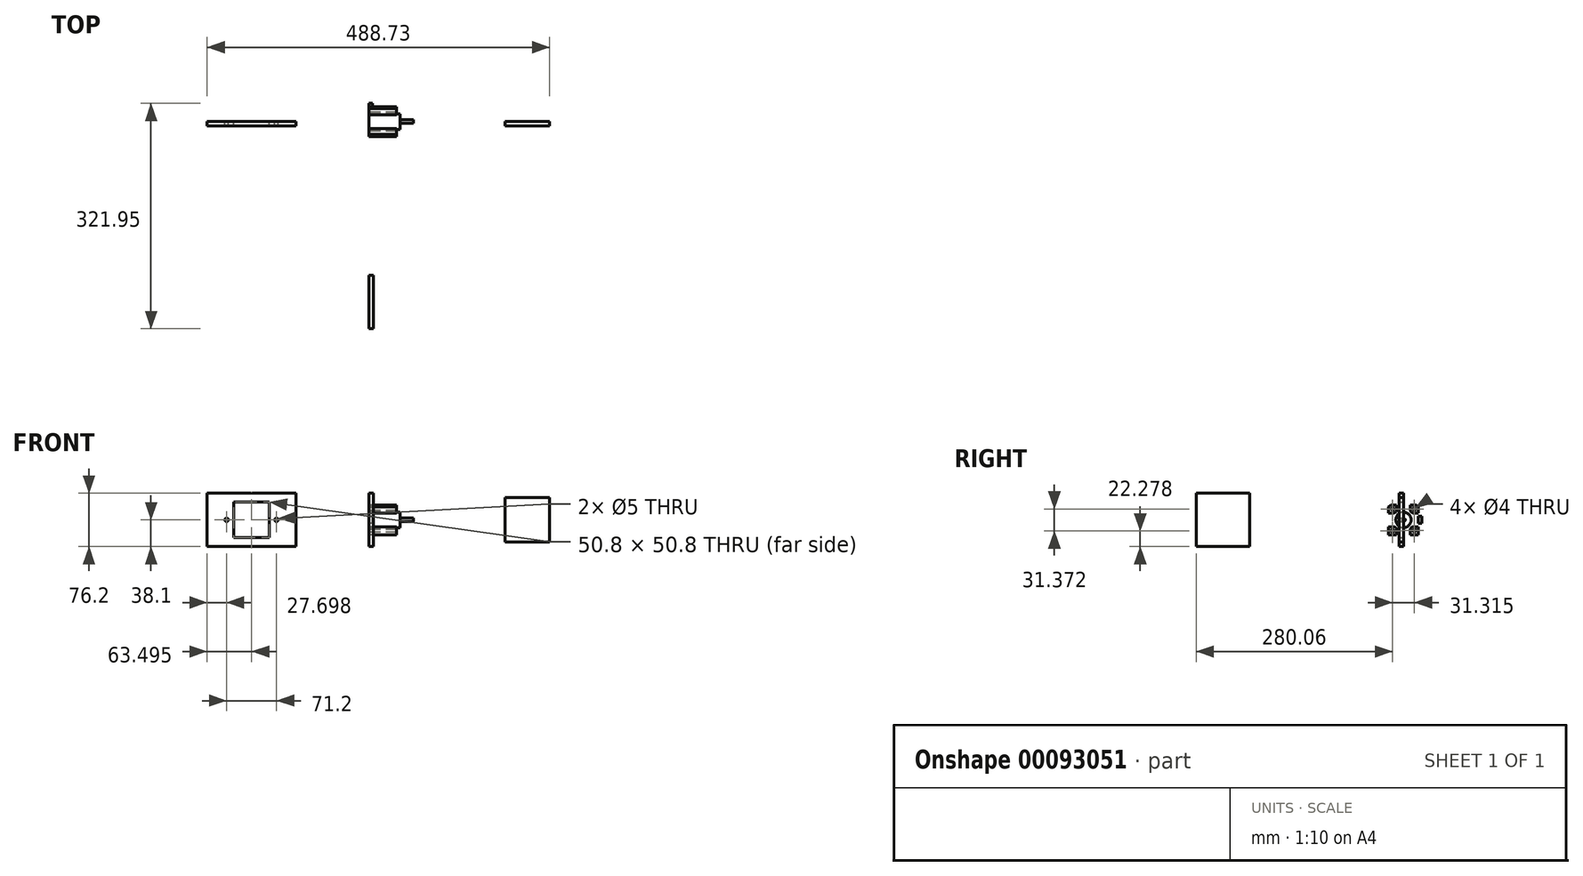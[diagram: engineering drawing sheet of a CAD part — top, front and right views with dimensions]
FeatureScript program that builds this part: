
annotation { "Feature Type Name" : "Feature", "Feature Type Description" : "" }
export const myFeature = defineFeature(function(context is Context, id is Id, definition is map)
    precondition{}
    {
        {
            var Q0;
            Q0=qCreatedBy(makeId("Right.planeOp"),FACE);
            var sketch = newSketch(context, id + "F0", { "sketchPlane" : qUnion([Q0])});
            skLineSegment(sketch, "E0.bottom", {"start": v(-21.15, -21.15) * mm, "end": v(21.15, -21.15) * mm});
            skLineSegment(sketch, "E0.top", {"start": v(-21.15, 21.15) * mm, "end": v(21.15, 21.15) * mm});
            skLineSegment(sketch, "E0.left", {"start": v(-21.15, -21.15) * mm, "end": v(-21.15, 21.15) * mm});
            skLineSegment(sketch, "E0.right", {"start": v(21.15, -21.15) * mm, "end": v(21.15, 21.15) * mm});
            skPoint(sketch, "E0.middle", {"position": v(0, 0) * mm});
            skCircle(sketch, "E1", {"center": v(0, 0) * mm, "radius": 2.5 * mm});
            skCircle(sketch, "E2", {"center": v(0, 0) * mm, "radius": 11 * mm});
            skLineSegment(sketch, "E3.bottom", {"start": v(21.15, 9.95) * mm, "end": v(13.76, 9.95) * mm});
            skLineSegment(sketch, "E3.top", {"start": v(21.15, 21.15) * mm, "end": v(9.95, 21.15) * mm});
            skLineSegment(sketch, "E3.left", {"start": v(21.15, 9.95) * mm, "end": v(21.15, 21.15) * mm});
            skLineSegment(sketch, "E3.right", {"start": v(9.95, 13.76) * mm, "end": v(9.95, 21.15) * mm});
            skPoint(sketch, "E3.middle", {"position": v(15.55, 15.55) * mm});
            skLineSegment(sketch, "E4.bottom", {"start": v(21.15, -21.15) * mm, "end": v(9.95, -21.15) * mm});
            skLineSegment(sketch, "E4.top", {"start": v(21.15, -9.95) * mm, "end": v(13.76, -9.95) * mm});
            skLineSegment(sketch, "E4.left", {"start": v(21.15, -21.15) * mm, "end": v(21.15, -9.95) * mm});
            skLineSegment(sketch, "E4.right", {"start": v(9.95, -21.15) * mm, "end": v(9.95, -13.76) * mm});
            skPoint(sketch, "E4.middle", {"position": v(15.55, -15.55) * mm});
            skLineSegment(sketch, "E5.bottom", {"start": v(-9.95, -21.15) * mm, "end": v(-21.15, -21.15) * mm});
            skLineSegment(sketch, "E5.top", {"start": v(-13.76, -9.95) * mm, "end": v(-21.15, -9.95) * mm});
            skLineSegment(sketch, "E5.left", {"start": v(-9.95, -21.15) * mm, "end": v(-9.95, -13.76) * mm});
            skLineSegment(sketch, "E5.right", {"start": v(-21.15, -21.15) * mm, "end": v(-21.15, -9.95) * mm});
            skPoint(sketch, "E5.middle", {"position": v(-15.55, -15.55) * mm});
            skLineSegment(sketch, "E6.bottom", {"start": v(-13.76, 9.95) * mm, "end": v(-21.15, 9.95) * mm});
            skLineSegment(sketch, "E6.top", {"start": v(-9.95, 21.15) * mm, "end": v(-21.15, 21.15) * mm});
            skLineSegment(sketch, "E6.left", {"start": v(-9.95, 13.76) * mm, "end": v(-9.95, 21.15) * mm});
            skLineSegment(sketch, "E6.right", {"start": v(-21.15, 9.95) * mm, "end": v(-21.15, 21.15) * mm});
            skPoint(sketch, "E6.middle", {"position": v(-15.55, 15.55) * mm});
            skPoint(sketch, "E7", {"position": v(21.15, 0) * mm});
            skLineSegment(sketch, "E8.bottom", {"start": v(26.15, -5) * mm, "end": v(21.15, -5) * mm});
            skLineSegment(sketch, "E8.top", {"start": v(26.15, 5) * mm, "end": v(21.15, 5) * mm});
            skLineSegment(sketch, "E8.left", {"start": v(26.15, -5) * mm, "end": v(26.15, 5) * mm});
            skLineSegment(sketch, "E8.right", {"start": v(21.15, -5) * mm, "end": v(21.15, 5) * mm});
            skPoint(sketch, "E8.middle", {"position": v(23.65, 0) * mm});
            skLineSegment(sketch, "E9", {"start": v(-18.35, 21.15) * mm, "end": v(-21.15, 18.35) * mm});
            skLineSegment(sketch, "E10", {"start": v(18.35, 21.15) * mm, "end": v(21.15, 18.35) * mm});
            skLineSegment(sketch, "E11", {"start": v(21.15, -18.35) * mm, "end": v(18.35, -21.15) * mm});
            skLineSegment(sketch, "E12", {"start": v(-21.15, -18.35) * mm, "end": v(-18.35, -21.15) * mm});
            skPoint(sketch, "E13.visualSharp", {"position": v(9.95, 9.95) * mm});
            skArc(sketch, "E13.filletArc", {"start": v(9.95, 13.76) * mm, "mid": v(11.07, 11.07) * mm, "end": v(13.76, 9.95) * mm});
            skPoint(sketch, "E14.visualSharp", {"position": v(9.95, -9.95) * mm});
            skArc(sketch, "E14.filletArc", {"start": v(13.76, -9.95) * mm, "mid": v(11.07, -11.07) * mm, "end": v(9.95, -13.76) * mm});
            skPoint(sketch, "E15.visualSharp", {"position": v(-9.95, -9.95) * mm});
            skArc(sketch, "E15.filletArc", {"start": v(-9.95, -13.76) * mm, "mid": v(-11.07, -11.07) * mm, "end": v(-13.76, -9.95) * mm});
            skPoint(sketch, "E16.visualSharp", {"position": v(-9.95, 9.95) * mm});
            skArc(sketch, "E16.filletArc", {"start": v(-13.76, 9.95) * mm, "mid": v(-11.07, 11.07) * mm, "end": v(-9.95, 13.76) * mm});
            skCircle(sketch, "E17", {"center": v(-15.55, 15.55) * mm, "radius": 2 * mm});
            skCircle(sketch, "E18", {"center": v(15.55, 15.55) * mm, "radius": 2 * mm});
            skCircle(sketch, "E19", {"center": v(15.58, -15.33) * mm, "radius": 2 * mm});
            skCircle(sketch, "E20", {"center": v(-15.74, -15.82) * mm, "radius": 2 * mm});
            skSolve(sketch);
        }
        {
            var Q0;
            {var subQ3=sQuery(id+"F0.wireOp",EDGE,"E3.bottom");Q0=makeQuery(id+"F0.imprint","IMPRINT",FACE,{"disambiguationData":[TD([[makeQuery(id+"F0.imprint","IMPRINT",EDGE,{"derivedFrom":subQ3}),-1.0]])]});}
            var Q1;
            {var subQ4=sQuery(id+"F0.wireOp",EDGE,"E4.top");Q1=makeQuery(id+"F0.imprint","IMPRINT",FACE,{"disambiguationData":[TD([[makeQuery(id+"F0.imprint","IMPRINT",EDGE,{"derivedFrom":subQ4}),1.0]])]});}
            var Q2;
            {var subQ1=sQuery(id+"F0.wireOp",EDGE,"E5.top");Q2=makeQuery(id+"F0.imprint","IMPRINT",FACE,{"disambiguationData":[TD([[makeQuery(id+"F0.imprint","IMPRINT",EDGE,{"derivedFrom":subQ1}),1.0]])]});}
            var Q3;
            {var subQ1=sQuery(id+"F0.wireOp",EDGE,"E6.bottom");Q3=makeQuery(id+"F0.imprint","IMPRINT",FACE,{"disambiguationData":[TD([[makeQuery(id+"F0.imprint","IMPRINT",EDGE,{"derivedFrom":subQ1}),-1.0]])]});}
            var Q4;
            Q4=makeQuery(id+"F0.imprint","IMPRINT",FACE,{"disambiguationData":[TD([[makeQuery(id+"F0.imprint","IMPRINT",EDGE,{"derivedFrom":sQuery(id+"F0.wireOp",EDGE,"E0.bottom")}),1.0]])]});
            var Q5;
            {var subQ1=sQuery(id+"F0.wireOp",EDGE,"E6.bottom");Q5=makeQuery(id+"F0.imprint","IMPRINT",FACE,{"disambiguationData":[TD([[makeQuery(id+"F0.imprint","IMPRINT",EDGE,{"derivedFrom":subQ1}),-1.0]])]});}
            var Q6;
            {var subQ3=sQuery(id+"F0.wireOp",EDGE,"E3.bottom");Q6=makeQuery(id+"F0.imprint","IMPRINT",FACE,{"disambiguationData":[TD([[makeQuery(id+"F0.imprint","IMPRINT",EDGE,{"derivedFrom":subQ3}),-1.0]])]});}
            var Q7;
            Q7=makeQuery(id+"F0.imprint","IMPRINT",FACE,{"disambiguationData":[TD([[makeQuery(id+"F0.imprint","IMPRINT",EDGE,{"derivedFrom":sQuery(id+"F0.wireOp",EDGE,"E1")}),-1.0]])]});
            var Q8;
            Q8=makeQuery(id+"F0.imprint","IMPRINT",FACE,{"disambiguationData":[TD([[makeQuery(id+"F0.imprint","IMPRINT",EDGE,{"derivedFrom":sQuery(id+"F0.wireOp",EDGE,"E1")}),1.0]])]});
            extrude(context, id + "F1", {"entities" : qUnion([Q0, Q1, Q2, Q3, Q4, Q5, Q6, Q7, Q8]), "depth" : 39 * mm});
        }
        {
            var Q0;
            Q0=makeQuery(id+"F0.imprint","IMPRINT",FACE,{"disambiguationData":[TD([[makeQuery(id+"F0.imprint","IMPRINT",EDGE,{"derivedFrom":sQuery(id+"F0.wireOp",EDGE,"E8.bottom")}),-1.0]])]});
            extrude(context, id + "F2", {"entities" : qUnion([Q0]), "operationType" : NewBodyOperationType.ADD, "depth" : 5 * mm});
        }
        {
            var Q0;
            Q0=makeQuery(id+"F0.imprint","IMPRINT",FACE,{"disambiguationData":[TD([[makeQuery(id+"F0.imprint","IMPRINT",EDGE,{"derivedFrom":sQuery(id+"F0.wireOp",EDGE,"E1")}),-1.0]])]});
            extrude(context, id + "F3", {"entities" : qUnion([Q0]), "operationType" : NewBodyOperationType.ADD, "depth" : 39 * mm + 5.5 * mm});
        }
        {
            var Q0;
            Q0=makeQuery(id+"F0.imprint","IMPRINT",FACE,{"disambiguationData":[TD([[makeQuery(id+"F0.imprint","IMPRINT",EDGE,{"derivedFrom":sQuery(id+"F0.wireOp",EDGE,"E1")}),1.0]])]});
            extrude(context, id + "F4", {"entities" : qUnion([Q0]), "operationType" : NewBodyOperationType.ADD, "depth" : (39 + 24) * mm});
        }
        {
            var Q0;
            Q0=qCreatedBy(makeId("Right.planeOp"),FACE);
            var sketch = newSketch(context, id + "F5", { "sketchPlane" : qUnion([Q0])});
            skLineSegment(sketch, "E21.bottom", {"start": v(-219.6, -38.1) * mm, "end": v(-295.8, -38.1) * mm});
            skLineSegment(sketch, "E21.top", {"start": v(-219.6, 38.1) * mm, "end": v(-295.8, 38.1) * mm});
            skLineSegment(sketch, "E21.left", {"start": v(-219.6, -38.1) * mm, "end": v(-219.6, 38.1) * mm});
            skLineSegment(sketch, "E21.right", {"start": v(-295.8, -38.1) * mm, "end": v(-295.8, 38.1) * mm});
            skPoint(sketch, "E21.middle", {"position": v(-257.7, 0) * mm});
            skSolve(sketch);
        }
        {
            var Q0;
            Q0 = qSketchRegion(id + "F5", true);
            extrude(context, id + "F6", {"entities" : qUnion([Q0]), "depth" : 6 * mm});
        }
        {
            var Q0;
            Q0=qCreatedBy(makeId("Front.planeOp"),FACE);
            var sketch = newSketch(context, id + "F7", { "sketchPlane" : qUnion([Q0])});
            skLineSegment(sketch, "E22.bottom", {"start": v(-104.05, -38.1) * mm, "end": v(-231.05, -38.1) * mm});
            skLineSegment(sketch, "E22.left", {"start": v(-104.05, -38.1) * mm, "end": v(-104.05, 38.1) * mm});
            skLineSegment(sketch, "E22.right", {"start": v(-231.05, -38.1) * mm, "end": v(-231.05, 38.1) * mm});
            skPoint(sketch, "E22.middle", {"position": v(-167.55, 0) * mm});
            skLineSegment(sketch, "E23", {"start": v(-104.05, 38.1) * mm, "end": v(-231.05, 38.1) * mm});
            skCircle(sketch, "E24", {"center": v(-203.35, 0) * mm, "radius": 2.5 * mm});
            skCircle(sketch, "E25", {"center": v(-132.15, 0) * mm, "radius": 2.5 * mm});
            skLineSegment(sketch, "E26.bottom", {"start": v(-192.95, -25.4) * mm, "end": v(-142.15, -25.4) * mm});
            skLineSegment(sketch, "E26.top", {"start": v(-192.95, 25.4) * mm, "end": v(-142.15, 25.4) * mm});
            skLineSegment(sketch, "E26.left", {"start": v(-192.95, -25.4) * mm, "end": v(-192.95, 25.4) * mm});
            skLineSegment(sketch, "E26.right", {"start": v(-142.15, -25.4) * mm, "end": v(-142.15, 25.4) * mm});
            skSolve(sketch);
        }
        {
            var Q0;
            Q0=makeQuery(id+"F7.imprint","IMPRINT",FACE,{"disambiguationData":[TD([[makeQuery(id+"F7.imprint","IMPRINT",EDGE,{"derivedFrom":sQuery(id+"F7.wireOp",EDGE,"E22.bottom")}),-1.0]])]});
            extrude(context, id + "F8", {"entities" : qUnion([Q0]), "depth" : 6 * mm});
        }
        {
            var Q0;
            Q0=qCreatedBy(makeId("Front.planeOp"),FACE);
            var sketch = newSketch(context, id + "F9", { "sketchPlane" : qUnion([Q0])});
            skLineSegment(sketch, "E27.bottom", {"start": v(257.68, -31.75) * mm, "end": v(194.18, -31.75) * mm});
            skLineSegment(sketch, "E27.top", {"start": v(257.68, 31.75) * mm, "end": v(194.18, 31.75) * mm});
            skLineSegment(sketch, "E27.left", {"start": v(257.68, -31.75) * mm, "end": v(257.68, 31.75) * mm});
            skLineSegment(sketch, "E27.right", {"start": v(194.18, -31.75) * mm, "end": v(194.18, 31.75) * mm});
            skPoint(sketch, "E27.middle", {"position": v(225.93, 0) * mm});
            skSolve(sketch);
        }
        {
            var Q0;
            Q0 = qSketchRegion(id + "F9", true);
            extrude(context, id + "F10", {"entities" : qUnion([Q0]), "depth" : 6 * mm});
        }
    });
